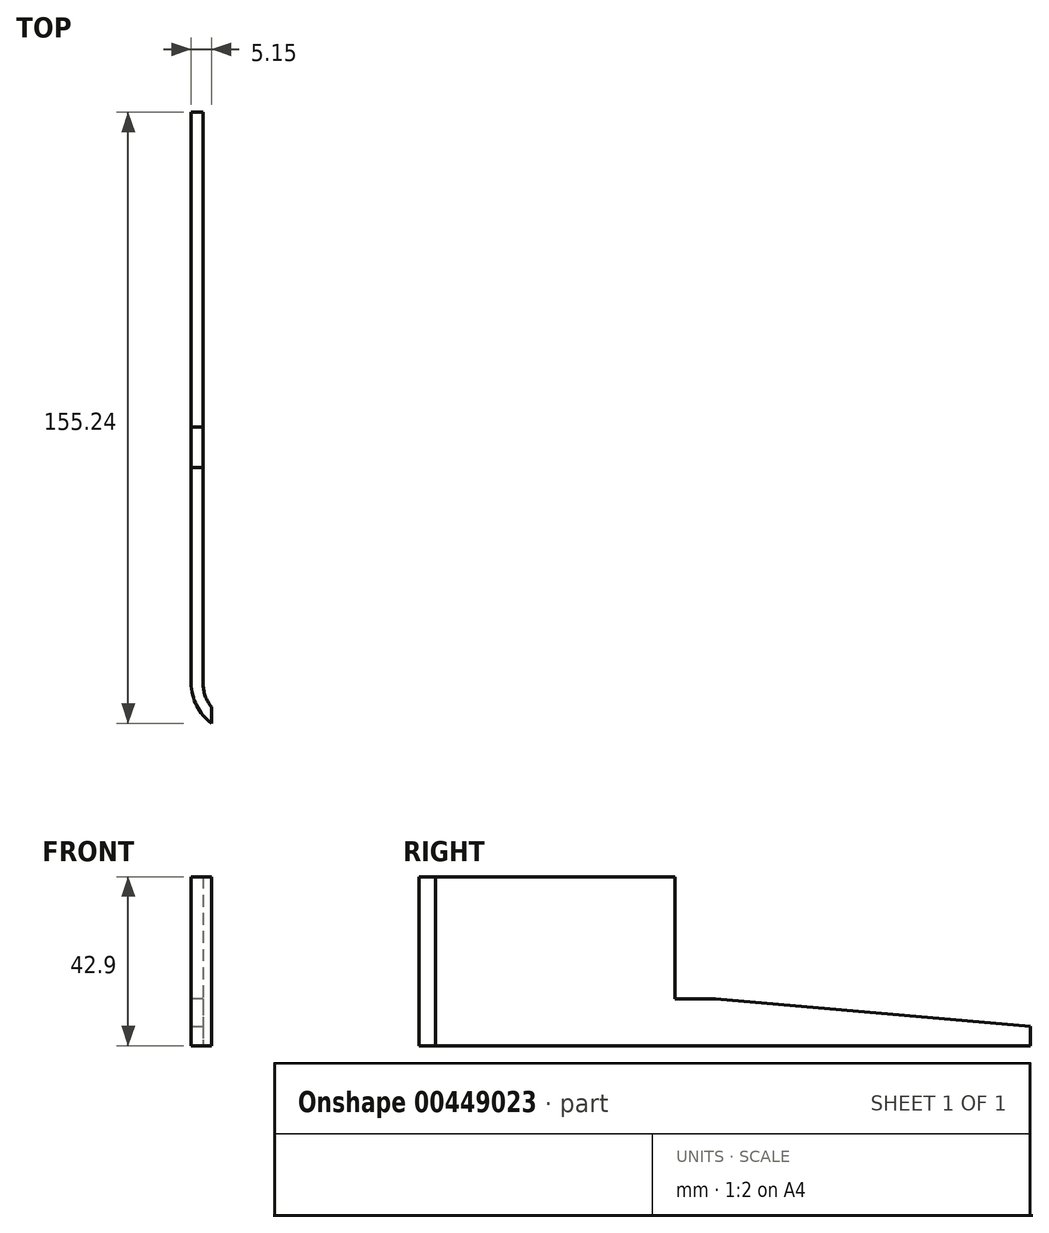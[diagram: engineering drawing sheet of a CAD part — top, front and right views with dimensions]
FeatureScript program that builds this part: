
annotation { "Feature Type Name" : "Feature", "Feature Type Description" : "" }
export const myFeature = defineFeature(function(context is Context, id is Id, definition is map)
    precondition{}
    {
        {
            var Q0;
            Q0=qCreatedBy(makeId("Top.planeOp"),FACE);
            var sketch = newSketch(context, id + "F0", { "sketchPlane" : qUnion([Q0])});
            skLineSegment(sketch, "E0.bottom", {"start": v(-3, 76.7) * mm, "end": v(0, 76.7) * mm});
            skLineSegment(sketch, "E0.left", {"start": v(-3, 76.7) * mm, "end": v(-3, -68.3) * mm});
            skLineSegment(sketch, "E0.right", {"start": v(0, 76.7) * mm, "end": v(0, -68.3) * mm});
            skArc(sketch, "E1", {"start": v(-3, -68.3) * mm, "mid": v(-1.64, -74.03) * mm, "end": v(2.15, -78.54) * mm});
            skArc(sketch, "E2", {"start": v(0, -68.3) * mm, "mid": v(0.55, -71.55) * mm, "end": v(2.15, -74.43) * mm});
            skLineSegment(sketch, "E3", {"start": v(2.15, -74.43) * mm, "end": v(2.15, -78.54) * mm});
            skSolve(sketch);
        }
        {
            var Q0;
            Q0 = qSketchRegion(id + "F0", true);
            extrude(context, id + "F1", {"entities" : qUnion([Q0]), "depth" : 11.9 * mm});
        }
        {
            var Q0;
            Q0=makeQuery(id+"F1.opExtrude","CAP_FACE",FACE,{"disambiguationData":[OSD([sQuery(id+"F0.wireOp",EDGE,"E0.bottom"),sQuery(id+"F0.wireOp",EDGE,"E0.top"),sQuery(id+"F0.wireOp",EDGE,"E0.left"),sQuery(id+"F0.wireOp",EDGE,"E0.right")])],"isStart":false});
            var sketch = newSketch(context, id + "F2", { "sketchPlane" : qUnion([Q0])});
            skLineSegment(sketch, "E4.bottom", {"start": v(-3, -13.5) * mm, "end": v(0, -13.5) * mm});
            skLineSegment(sketch, "E4.top", {"start": v(-3, 76.7) * mm, "end": v(0, 76.7) * mm});
            skLineSegment(sketch, "E4.left", {"start": v(-3, 76.7) * mm, "end": v(-3, -13.5) * mm});
            skLineSegment(sketch, "E4.right", {"start": v(0, 76.7) * mm, "end": v(0, -13.5) * mm});
            skSolve(sketch);
        }
        {
            var Q0;
            {var subQ2=sQuery(id+"F2.wireOp",EDGE,"E4.bottom");Q0=makeQuery(id+"F2.imprint","IMPRINT",FACE,{"disambiguationData":[TD([[makeQuery(id+"F2.imprint","IMPRINT",EDGE,{"derivedFrom":subQ2}),-1.0]])]});}
            extrude(context, id + "F3", {"entities" : qUnion([Q0]), "operationType" : NewBodyOperationType.ADD, "depth" : 31 * mm});
        }
        {
            var Q0;
            Q0=makeQuery(id+"F1.opExtrude","CAP_EDGE",EDGE,{"disambiguationData":[OSD([sQuery(id+"F0.wireOp",EDGE,"E0.bottom")])],"isStart":false});
            chamfer(context, id + "F4", {"entities" : qUnion([Q0]), "chamferType" : ChamferType.OFFSET_ANGLE, "width" : 7 * mm, "oppositeDirection" : false, "angle" : 85 * degree, "tangentPropagation" : true});
        }
    });
